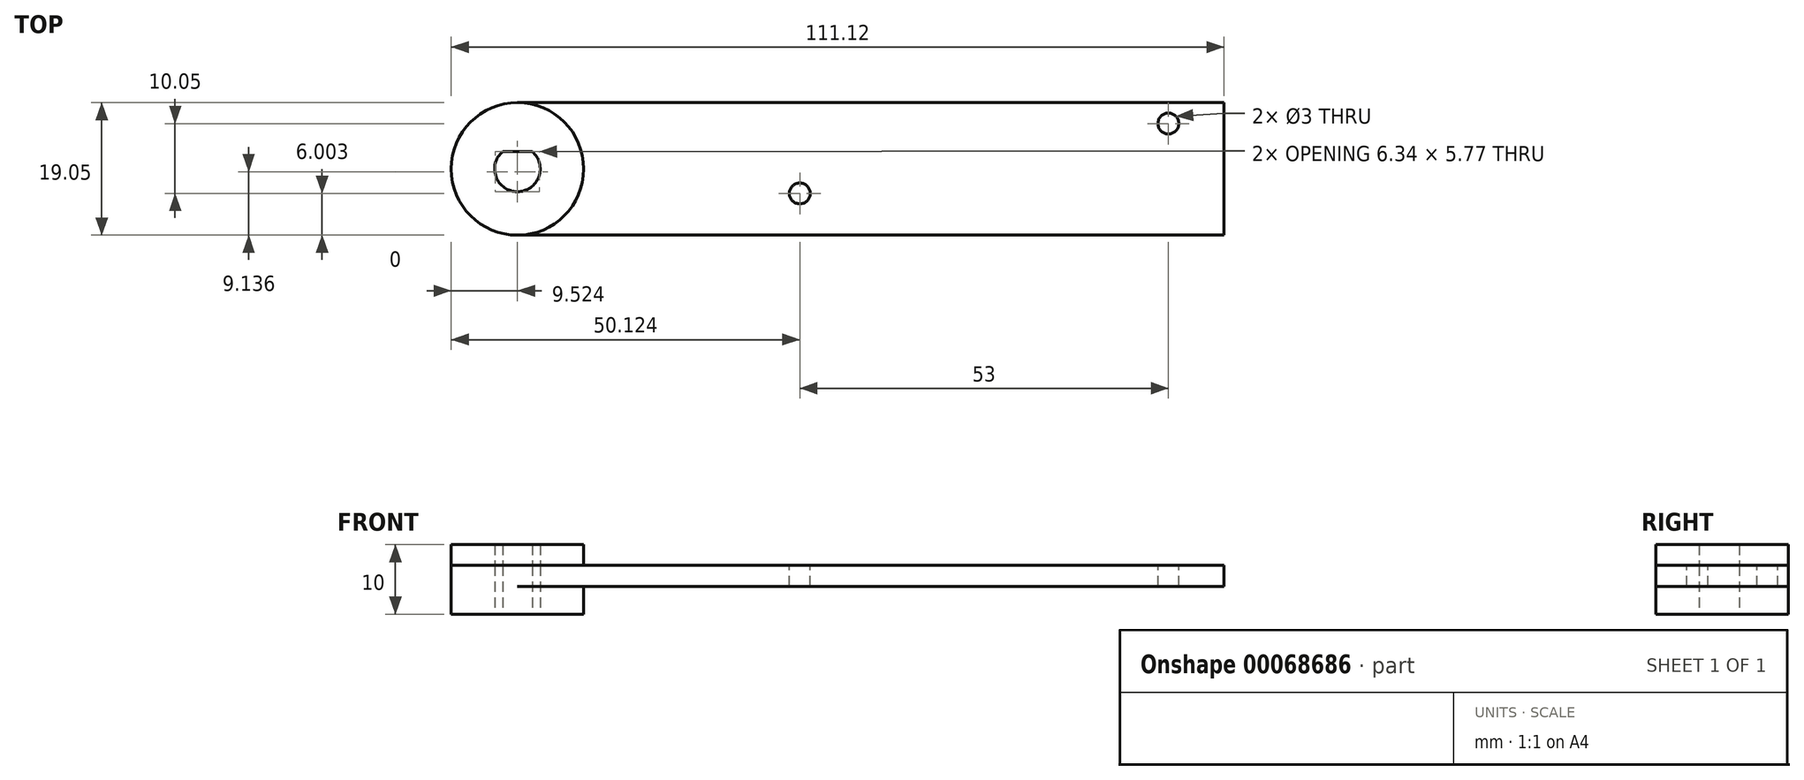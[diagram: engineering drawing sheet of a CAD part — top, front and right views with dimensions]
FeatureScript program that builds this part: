
annotation { "Feature Type Name" : "Feature", "Feature Type Description" : "" }
export const myFeature = defineFeature(function(context is Context, id is Id, definition is map)
    precondition{}
    {
        {
            var Q0;
            Q0=qCreatedBy(makeId("Top.planeOp"),FACE);
            var sketch = newSketch(context, id + "F0", { "sketchPlane" : qUnion([Q0])});
            skArc(sketch, "E0", {"start": v(-57.04, -25) * mm, "mid": v(-66.56, -34.52) * mm, "end": v(-57.04, -44.05) * mm});
            skLineSegment(sketch, "E1", {"start": v(-57.04, -44.05) * mm, "end": v(-57.04, -25) * mm, "construction": true});
            skPoint(sketch, "E1.startSnap0", {"position": v(-57.04, -37.53) * mm});
            skLineSegment(sketch, "E2", {"start": v(-57.04, -25) * mm, "end": v(44.56, -25) * mm});
            skLineSegment(sketch, "E3", {"start": v(-57.04, -44.05) * mm, "end": v(44.56, -44.05) * mm});
            skLineSegment(sketch, "E4", {"start": v(44.56, -25) * mm, "end": v(44.56, -44.05) * mm});
            skArc(sketch, "E5", {"start": v(-59.16, -32.03) * mm, "mid": v(-57.04, -37.8) * mm, "end": v(-54.9, -32.03) * mm});
            skLineSegment(sketch, "E6", {"start": v(-59.16, -32.03) * mm, "end": v(-54.9, -32.03) * mm});
            skSolve(sketch);
        }
        {
            var Q0;
            Q0=makeQuery(id+"F0.imprint","IMPRINT",FACE,{"disambiguationData":[TD([[makeQuery(id+"F0.imprint","IMPRINT",EDGE,{"derivedFrom":sQuery(id+"F0.wireOp",EDGE,"25f2d6ab-122a-4e37-bb55-a601b16a11c0.1")}),-1.0]])]});
            var Q1;
            Q1=makeQuery(id+"F0.imprint","IMPRINT",FACE,{"disambiguationData":[TD([[makeQuery(id+"F0.imprint","IMPRINT",EDGE,{"derivedFrom":sQuery(id+"F0.wireOp",EDGE,"E0")}),1.0]])]});
            extrude(context, id + "F1", {"entities" : qUnion([Q0, Q1]), "depth" : 3 * mm});
        }
        {
            var Q0;
            Q0=makeQuery(id+"F1.opExtrude","CAP_FACE",FACE,{"disambiguationData":[OSD([sQuery(id+"F0.wireOp",EDGE,"25f2d6ab-122a-4e37-bb55-a601b16a11c0.1"),sQuery(id+"F0.wireOp",EDGE,"25f2d6ab-122a-4e37-bb55-a601b16a11c0.2"),sQuery(id+"F0.wireOp",EDGE,"E0"),sQuery(id+"F0.wireOp",EDGE,"E2"),sQuery(id+"F0.wireOp",EDGE,"E3"),sQuery(id+"F0.wireOp",EDGE,"E4")])],"isStart":false});
            var sketch = newSketch(context, id + "F2", { "sketchPlane" : qUnion([Q0])});
            skCircle(sketch, "E7", {"center": v(36.56, -28) * mm, "radius": 1.5 * mm});
            skCircle(sketch, "E8", {"center": v(-16.44, -38.05) * mm, "radius": 1.5 * mm});
            skLineSegment(sketch, "E9", {"start": v(44.56, -34.52) * mm, "end": v(-66.56, -34.52) * mm, "construction": true});
            skSolve(sketch);
        }
        {
            var Q0;
            Q0 = qSketchRegion(id + "F2", true);
            extrude(context, id + "F3", {"entities" : qUnion([Q0]), "operationType" : NewBodyOperationType.REMOVE, "oppositeDirection" : true, "depth" : 3 * mm});
        }
        {
            var Q0;
            Q0=makeQuery(id+"F0.imprint","IMPRINT",FACE,{"disambiguationData":[TD([[makeQuery(id+"F0.imprint","IMPRINT",EDGE,{"derivedFrom":sQuery(id+"F0.wireOp",EDGE,"E0")}),1.0]])]});
            var sketch = newSketch(context, id + "F4", { "sketchPlane" : qUnion([Q0])});
            skCircle(sketch, "E10", {"center": v(-57.04, -34.52) * mm, "radius": 9.52 * mm});
            skArc(sketch, "E11.0", {"start": v(-59.16, -32.03) * mm, "mid": v(-57.04, -37.8) * mm, "end": v(-54.9, -32.03) * mm});
            skLineSegment(sketch, "E12.0", {"start": v(-59.16, -32.03) * mm, "end": v(-54.9, -32.03) * mm});
            skSolve(sketch);
        }
        {
            var Q0;
            Q0 = qSketchRegion(id + "F4", true);
            extrude(context, id + "F5", {"entities" : qUnion([Q0]), "operationType" : NewBodyOperationType.ADD, "oppositeDirection" : true, "depth" : 4 * mm});
        }
        {
            var Q0;
            Q0=makeQuery(id+"F1.opExtrude","CAP_FACE",FACE,{"disambiguationData":[OSD([sQuery(id+"F0.wireOp",EDGE,"25f2d6ab-122a-4e37-bb55-a601b16a11c0.1"),sQuery(id+"F0.wireOp",EDGE,"25f2d6ab-122a-4e37-bb55-a601b16a11c0.2"),sQuery(id+"F0.wireOp",EDGE,"E0"),sQuery(id+"F0.wireOp",EDGE,"E2"),sQuery(id+"F0.wireOp",EDGE,"E3"),sQuery(id+"F0.wireOp",EDGE,"E4")])],"isStart":false});
            var sketch = newSketch(context, id + "F6", { "sketchPlane" : qUnion([Q0])});
            skPoint(sketch, "E13.2", {"position": v(-57.04, -34.52) * mm});
            skCircle(sketch, "E14", {"center": v(-57.04, -34.52) * mm, "radius": 9.52 * mm});
            skArc(sketch, "E15.0", {"start": v(-59.16, -32.03) * mm, "mid": v(-57.04, -37.8) * mm, "end": v(-54.9, -32.03) * mm});
            skLineSegment(sketch, "E15.1", {"start": v(-59.16, -32.03) * mm, "end": v(-54.9, -32.03) * mm});
            skSolve(sketch);
        }
        {
            var Q0;
            Q0 = qSketchRegion(id + "F6", true);
            extrude(context, id + "F7", {"entities" : qUnion([Q0]), "depth" : 3 * mm});
        }
    });
